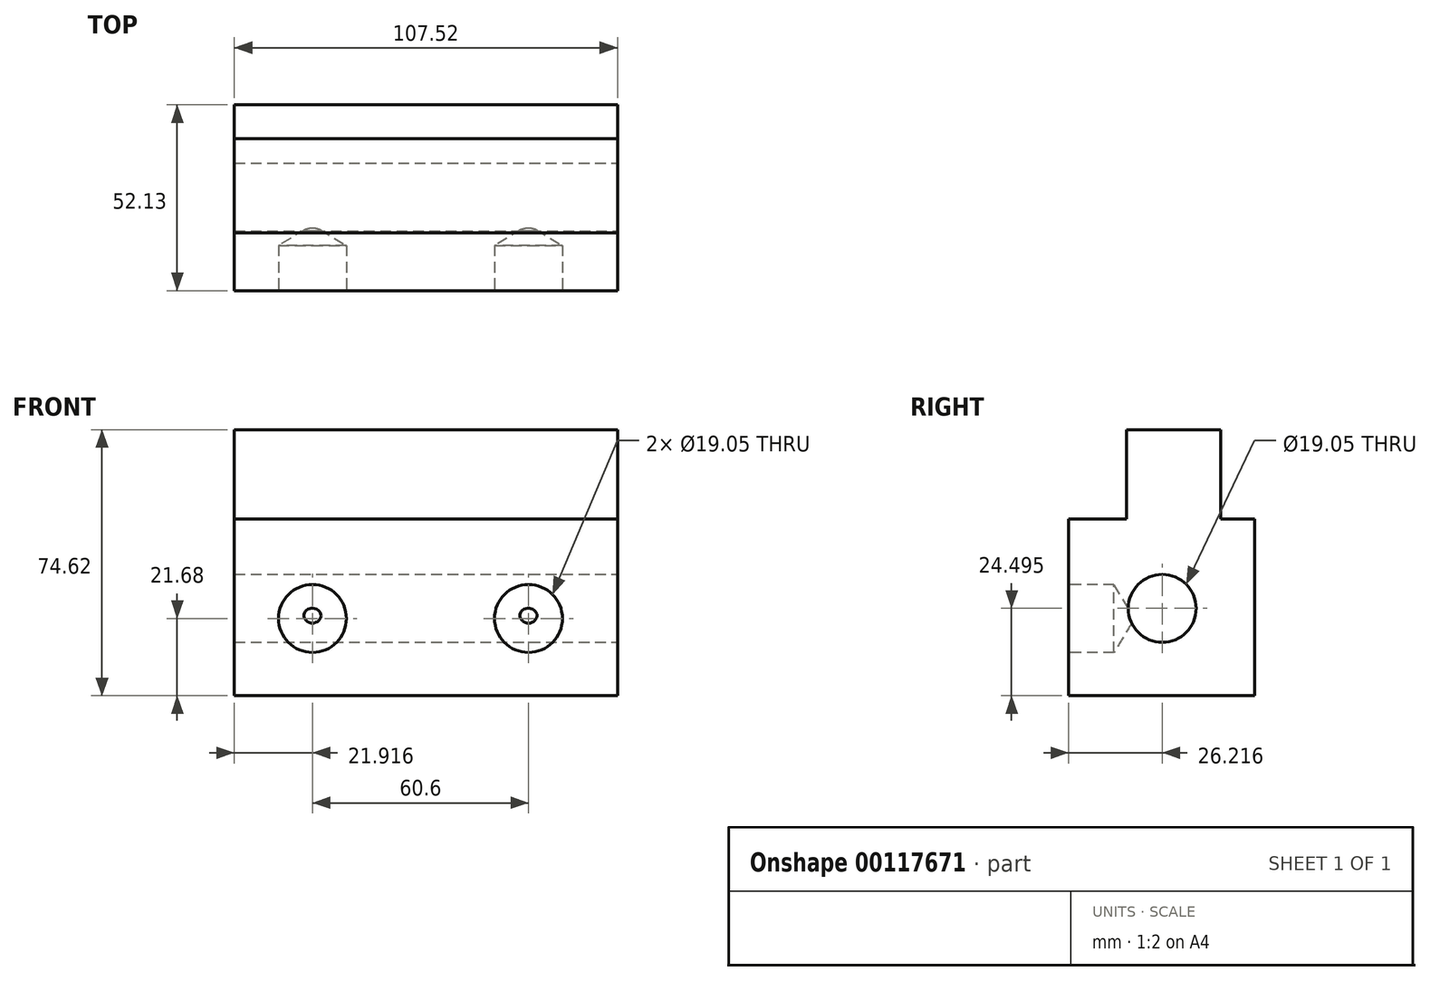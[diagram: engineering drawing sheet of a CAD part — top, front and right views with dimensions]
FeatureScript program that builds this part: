
annotation { "Feature Type Name" : "Feature", "Feature Type Description" : "" }
export const myFeature = defineFeature(function(context is Context, id is Id, definition is map)
    precondition{}
    {
        {
            var Q0;
            Q0=qCreatedBy(makeId("Top.planeOp"),FACE);
            var sketch = newSketch(context, id + "F0", { "sketchPlane" : qUnion([Q0])});
            skLineSegment(sketch, "E0.bottom", {"start": v(-53.92, 39.99) * mm, "end": v(53.6, 39.99) * mm});
            skLineSegment(sketch, "E0.top", {"start": v(-53.92, -12.14) * mm, "end": v(53.6, -12.14) * mm});
            skLineSegment(sketch, "E0.left", {"start": v(-53.92, 39.99) * mm, "end": v(-53.92, -12.14) * mm});
            skLineSegment(sketch, "E0.right", {"start": v(53.6, 39.99) * mm, "end": v(53.6, -12.14) * mm});
            skSolve(sketch);
        }
        {
            var Q0;
            Q0=makeQuery(id+"F0.imprint","IMPRINT",FACE,{"disambiguationData":[TD([[makeQuery(id+"F0.imprint","IMPRINT",EDGE,{"derivedFrom":sQuery(id+"F0.wireOp",EDGE,"E0.bottom")}),-1.0]])]});
            extrude(context, id + "F1", {"entities" : qUnion([Q0]), "depth" : 49.57 * mm});
        }
        {
            var Q0;
            Q0=makeQuery(id+"F1.opExtrude","CAP_FACE",FACE,{"disambiguationData":[OSD([sQuery(id+"F0.wireOp",EDGE,"E0.bottom"),sQuery(id+"F0.wireOp",EDGE,"E0.top"),sQuery(id+"F0.wireOp",EDGE,"E0.left"),sQuery(id+"F0.wireOp",EDGE,"E0.right")])],"isStart":false});
            var sketch = newSketch(context, id + "F2", { "sketchPlane" : qUnion([Q0])});
            skLineSegment(sketch, "E1.bottom", {"start": v(-53.92, 30.47) * mm, "end": v(53.6, 30.47) * mm});
            skLineSegment(sketch, "E1.top", {"start": v(-53.92, 4.07) * mm, "end": v(53.6, 4.07) * mm});
            skLineSegment(sketch, "E1.left", {"start": v(-53.92, 30.47) * mm, "end": v(-53.92, 4.07) * mm});
            skLineSegment(sketch, "E1.right", {"start": v(53.6, 30.47) * mm, "end": v(53.6, 4.07) * mm});
            skSolve(sketch);
        }
        {
            var Q0;
            Q0=makeQuery(id+"F2.imprint","IMPRINT",FACE,{"disambiguationData":[TD([[makeQuery(id+"F2.imprint","IMPRINT",EDGE,{"derivedFrom":sQuery(id+"F2.wireOp",EDGE,"E1.bottom")}),-1.0]])]});
            extrude(context, id + "F3", {"entities" : qUnion([Q0]), "operationType" : NewBodyOperationType.ADD, "depth" : 25.05 * mm});
        }
        {
            var Q0;
            Q0=makeQuery(id+"F1.opExtrude","SWEPT_FACE",FACE,{"disambiguationData":[OSD([sQuery(id+"F0.wireOp",EDGE,"E0.top")])]});
            var sketch = newSketch(context, id + "F4", { "sketchPlane" : qUnion([Q0])});
            skCircle(sketch, "E2", {"center": v(-32, 21.68) * mm, "radius": 15.88 * mm});
            skCircle(sketch, "E3", {"center": v(28.6, 21.68) * mm, "radius": 15.88 * mm});
            skSolve(sketch);
        }
        {
            var Q0;
            Q0=makeQuery(id+"F3.boolean.opBoolean","MERGE",FACE,{"derivedFrom":[makeQuery(id+"F1.opExtrude","SWEPT_FACE",FACE,{"disambiguationData":[OSD([sQuery(id+"F0.wireOp",EDGE,"E0.right")])]}),makeQuery(id+"F3.opExtrude","SWEPT_FACE",FACE,{"disambiguationData":[OSD([sQuery(id+"F2.wireOp",EDGE,"E1.right")])]})]});
            var sketch = newSketch(context, id + "F5", { "sketchPlane" : qUnion([Q0])});
            skCircle(sketch, "E4", {"center": v(14.08, 24.5) * mm, "radius": 9.53 * mm});
            skSolve(sketch);
        }
        {
            var Q0;
            Q0=sQuery(id+"F5.wireOp",VERTEX,"E4.center");
            var Q1;
            Q1=makeQuery(id+"F1.opExtrude","SWEPT_BODY",BODY,{"disambiguationData":[OSD([sQuery(id+"F0.wireOp",EDGE,"E0.bottom"),sQuery(id+"F0.wireOp",EDGE,"E0.top"),sQuery(id+"F0.wireOp",EDGE,"E0.left"),sQuery(id+"F0.wireOp",EDGE,"E0.right")])]});
            hole(context, id + "F6", {"style" : HoleStyle.SIMPLE, "endStyle" : HoleEndStyle.THROUGH, "holeDiameter" : 19.05 * mm, "locations" : qUnion([Q0]), "scope" : qUnion([Q1]), "isTappedThrough" : true});
        }
        {
            var Q0;
            Q0=sQuery(id+"F4.wireOp",VERTEX,"E2.center");
            var Q1;
            Q1=sQuery(id+"F4.wireOp",VERTEX,"E3.center");
            var Q2;
            Q2=makeQuery(id+"F1.opExtrude","SWEPT_BODY",BODY,{"disambiguationData":[OSD([sQuery(id+"F0.wireOp",EDGE,"E0.bottom"),sQuery(id+"F0.wireOp",EDGE,"E0.top"),sQuery(id+"F0.wireOp",EDGE,"E0.left"),sQuery(id+"F0.wireOp",EDGE,"E0.right")])]});
            hole(context, id + "F7", {"style" : HoleStyle.SIMPLE, "endStyle" : HoleEndStyle.BLIND, "holeDiameter" : 19.05 * mm, "holeDepth" : 12.7 * mm, "locations" : qUnion([Q0, Q1]), "scope" : qUnion([Q2])});
        }
    });
